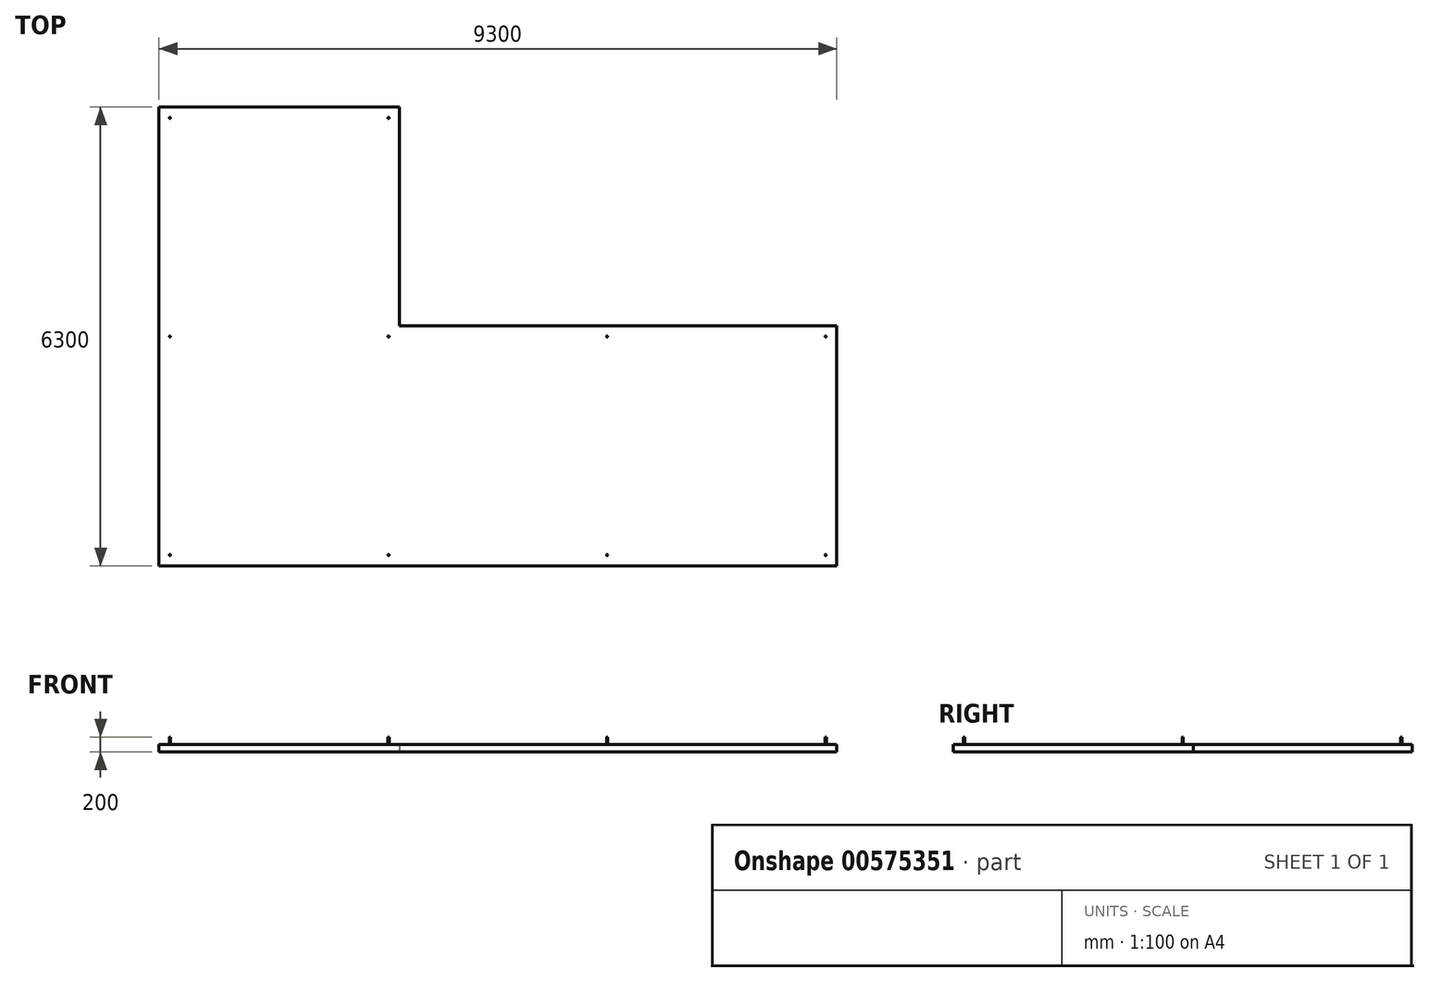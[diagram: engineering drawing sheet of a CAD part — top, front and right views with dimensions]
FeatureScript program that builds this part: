
annotation { "Feature Type Name" : "Feature", "Feature Type Description" : "" }
export const myFeature = defineFeature(function(context is Context, id is Id, definition is map)
    precondition{}
    {
        {
            var Q0;
            Q0=qCreatedBy(makeId("Top.planeOp"),FACE);
            var sketch = newSketch(context, id + "F0", { "sketchPlane" : qUnion([Q0])});
            skLineSegment(sketch, "E0", {"start": v(-150, -150) * mm, "end": v(-150, 6150) * mm});
            skLineSegment(sketch, "E1", {"start": v(-150, 6150) * mm, "end": v(3150, 6150) * mm});
            skLineSegment(sketch, "E2", {"start": v(3150, 6150) * mm, "end": v(3150, 3150) * mm});
            skLineSegment(sketch, "E3", {"start": v(3150, 3150) * mm, "end": v(9150, 3150) * mm});
            skLineSegment(sketch, "E4", {"start": v(9150, 3150) * mm, "end": v(9150, -150) * mm});
            skLineSegment(sketch, "E5", {"start": v(9150, -150) * mm, "end": v(-150, -150) * mm});
            skSolve(sketch);
        }
        {
            var Q0;
            Q0 = qSketchRegion(id + "F0", true);
            extrude(context, id + "F1", {"entities" : qUnion([Q0]), "depth" : 100 * mm, "offsetDistance" : 25 * mm});
        }
        {
            var Q0;
            Q0=makeQuery(id+"F1.opExtrude","CAP_FACE",FACE,{"disambiguationData":[OSD([sQuery(id+"F0.wireOp",EDGE,"E0"),sQuery(id+"F0.wireOp",EDGE,"E1"),sQuery(id+"F0.wireOp",EDGE,"E2"),sQuery(id+"F0.wireOp",EDGE,"E3"),sQuery(id+"F0.wireOp",EDGE,"E4"),sQuery(id+"F0.wireOp",EDGE,"E5")])],"isStart":false});
            var sketch = newSketch(context, id + "F2", { "sketchPlane" : qUnion([Q0])});
            skPoint(sketch, "E6", {"position": v(9000, 0) * mm});
            skCircle(sketch, "E7", {"center": v(9000, 0) * mm, "radius": 8 * mm});
            skCircle(sketch, "E8.0.1.0", {"center": v(9000, 3000) * mm, "radius": 8 * mm});
            skCircle(sketch, "E8.1.0.0", {"center": v(6000, 0) * mm, "radius": 8 * mm});
            skCircle(sketch, "E8.1.1.0", {"center": v(6000, 3000) * mm, "radius": 8 * mm});
            skCircle(sketch, "E8.2.0.0", {"center": v(3000, 0) * mm, "radius": 8 * mm});
            skCircle(sketch, "E8.2.1.0", {"center": v(3000, 3000) * mm, "radius": 8 * mm});
            skCircle(sketch, "E8.3.0.0", {"center": v(0, 0) * mm, "radius": 8 * mm});
            skCircle(sketch, "E8.3.1.0", {"center": v(0, 3000) * mm, "radius": 8 * mm});
            skLineSegment(sketch, "E8.direction1", {"start": v(9000, 0) * mm, "end": v(6000, 0) * mm, "construction": true});
            skLineSegment(sketch, "E8.direction2", {"start": v(9000, 0) * mm, "end": v(9000, 3000) * mm, "construction": true});
            skCircle(sketch, "E9.0.1.0", {"center": v(3000, 6000) * mm, "radius": 8 * mm});
            skCircle(sketch, "E9.0.1.1", {"center": v(0, 6000) * mm, "radius": 8 * mm});
            skLineSegment(sketch, "E9.direction1", {"start": v(0, 3000) * mm, "end": v(25, 3000) * mm, "construction": true});
            skLineSegment(sketch, "E9.direction2", {"start": v(0, 3000) * mm, "end": v(0, 6000) * mm, "construction": true});
            skSolve(sketch);
        }
        {
            var Q0;
            Q0 = qSketchRegion(id + "F2", true);
            extrude(context, id + "F3", {"entities" : qUnion([Q0]), "operationType" : NewBodyOperationType.ADD, "depth" : 100 * mm, "offsetDistance" : 25 * mm});
        }
    });
